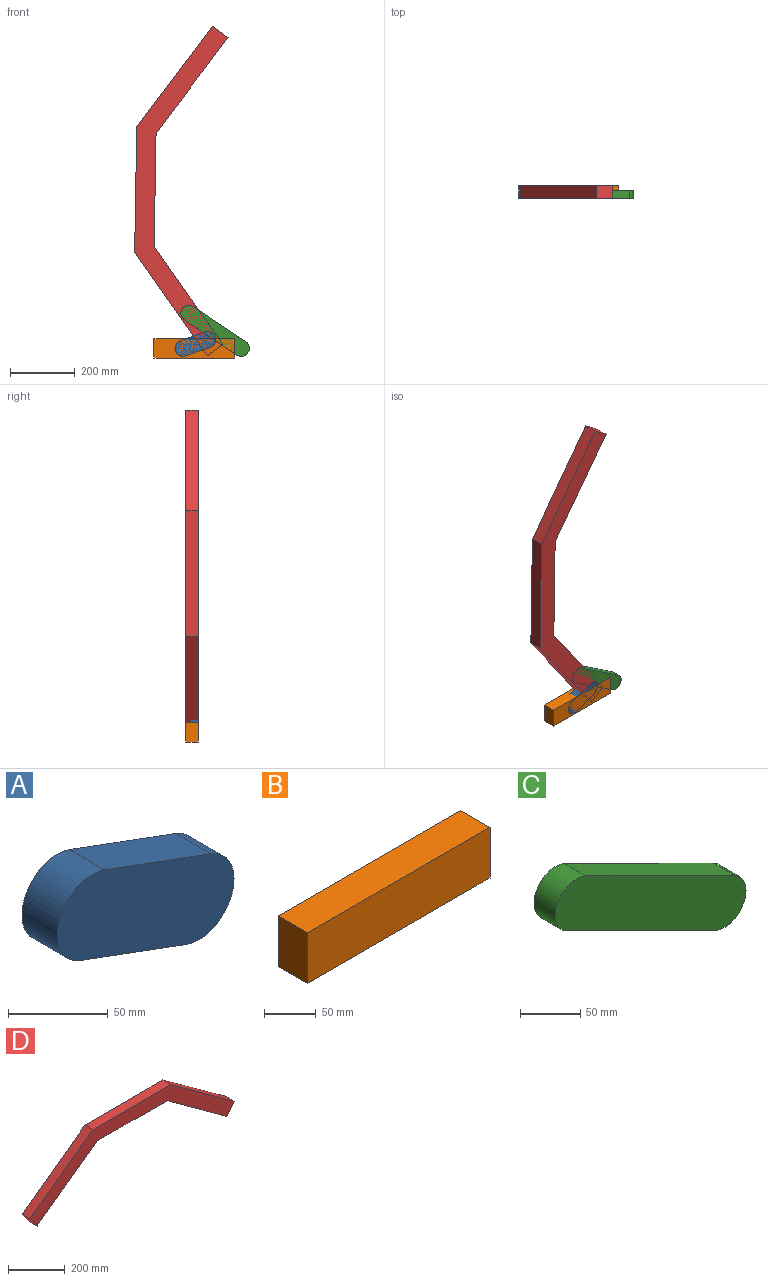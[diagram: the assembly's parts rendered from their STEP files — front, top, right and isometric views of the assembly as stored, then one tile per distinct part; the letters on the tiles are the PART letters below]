
ASSEMBLY  parts=4 mates=4
PART A: 6 faces, bbox 125.3x25x77.8 mm
  f0: plane 75.27x27.78mm, normal (0.35,0,0.94), area 2005.9mm2, adj f1,f3,f4,f5
  f1: cylinder r=25mm len=48.45mm, axis (0,1,0), area 1963.5mm2, adj f0,f2,f4,f5
  f2: plane 75.27x27.78mm, normal (-0.35,0,-0.94), area 2005.9mm2, adj f1,f3,f4,f5
  f3: cylinder r=25mm len=48.45mm, axis (0,1,0), area 1963.5mm2, adj f0,f2,f4,f5
  f4: plane 125.27x77.78mm, normal (0,-1,0), area 5975.3mm2, adj f0,f1,f2,f3
  f5: plane 125.27x77.78mm, normal (0,1,0), area 5975.3mm2, adj f0,f1,f2,f3
PART B: 6 faces, bbox 250x40x60 mm
  f0: plane 250x40mm, normal (0,0,1), area 10000mm2, adj f1,f3,f4,f5
  f1: plane 60x40mm, normal (-1,0,0), area 2400mm2, adj f0,f2,f4,f5
  f2: plane 250x40mm, normal (0,0,-1), area 10000mm2, adj f1,f3,f4,f5
  f3: plane 60x40mm, normal (1,0,0), area 2400mm2, adj f0,f2,f4,f5
  f4: plane 250x60mm, normal (0,-1,0), area 15000mm2, adj f0,f1,f2,f3
  f5: plane 250x60mm, normal (0,1,0), area 15000mm2, adj f0,f1,f2,f3
PART C: 6 faces, bbox 224.4x25x136.6 mm
  f0: plane 174.37x86.56mm, normal (-0.44,0,-0.9), area 4866.9mm2, adj f1,f3,f4,f5
  f1: cylinder r=25mm len=47.39mm, axis (0,1,0), area 1963.5mm2, adj f0,f2,f4,f5
  f2: plane 174.37x86.56mm, normal (0.44,0,0.9), area 4866.9mm2, adj f1,f3,f4,f5
  f3: cylinder r=25mm len=47.39mm, axis (0,1,0), area 1963.5mm2, adj f0,f2,f4,f5
  f4: plane 224.37x136.56mm, normal (0,-1,0), area 11697.2mm2, adj f0,f1,f2,f3
  f5: plane 224.37x136.56mm, normal (0,1,0), area 11697.2mm2, adj f0,f1,f2,f3
PART D: 10 faces, bbox 1020.8x40x277.7 mm
  f0: plane 48.54x40mm, normal (-0.81,0,-0.59), area 2400mm2, adj f1,f7,f8,f9
  f1: plane 299.67x217.72mm, normal (0.59,0,-0.81), area 14816.3mm2, adj f0,f2,f8,f9
  f2: plane 350.91x40mm, normal (0,0,-1), area 14036.5mm2, adj f1,f3,f8,f9
  f3: plane 299.67x217.72mm, normal (-0.59,0,-0.81), area 14816.3mm2, adj f2,f4,f8,f9
  f4: plane 48.54x40mm, normal (0.81,0,-0.59), area 2400mm2, adj f3,f5,f8,f9
  f5: plane 315.44x229.18mm, normal (0.59,0,0.81), area 15596.1mm2, adj f4,f6,f8,f9
  f6: plane 389.9x40mm, normal (0,0,1), area 15596.1mm2, adj f5,f7,f8,f9
  f7: plane 315.44x229.18mm, normal (-0.59,0,0.81), area 15596.1mm2, adj f0,f6,f8,f9
  f8: plane 1020.78x277.72mm, normal (0,-1,0), area 67843.2mm2, adj f0,f1,f2,f3,f4,f5,f6,f7
  f9: plane 1020.78x277.72mm, normal (0,1,0), area 67843.2mm2, adj f0,f1,f2,f3,f4,f5,f6,f7
PLACE A rot(axis=(0,1,0),140.4deg) t=(-390.05,65,-296.2)mm
PLACE B t=(225.12,40,134.93)mm
PLACE C rot(axis=(0,1,0),7.4deg) t=(236.98,65,107.51)mm
PLACE D rot(axis=(0,-1,0),89.1deg) t=(-153.79,40,518.14)mm
MATE revolute A.f3 <-> B.f4  axis (0,-1,0) through (-160,0,30)mm
MATE revolute C.f1 <-> B.f4  axis (0,-1,0) through (20,0,30)mm
MATE revolute D.f8 <-> C.f3  axis (0,-1,0) through (-141.71,0,138.39)mm
MATE revolute D.f8 <-> A.f1  axis (0,-1,0) through (-84.28,0,56.53)mm
